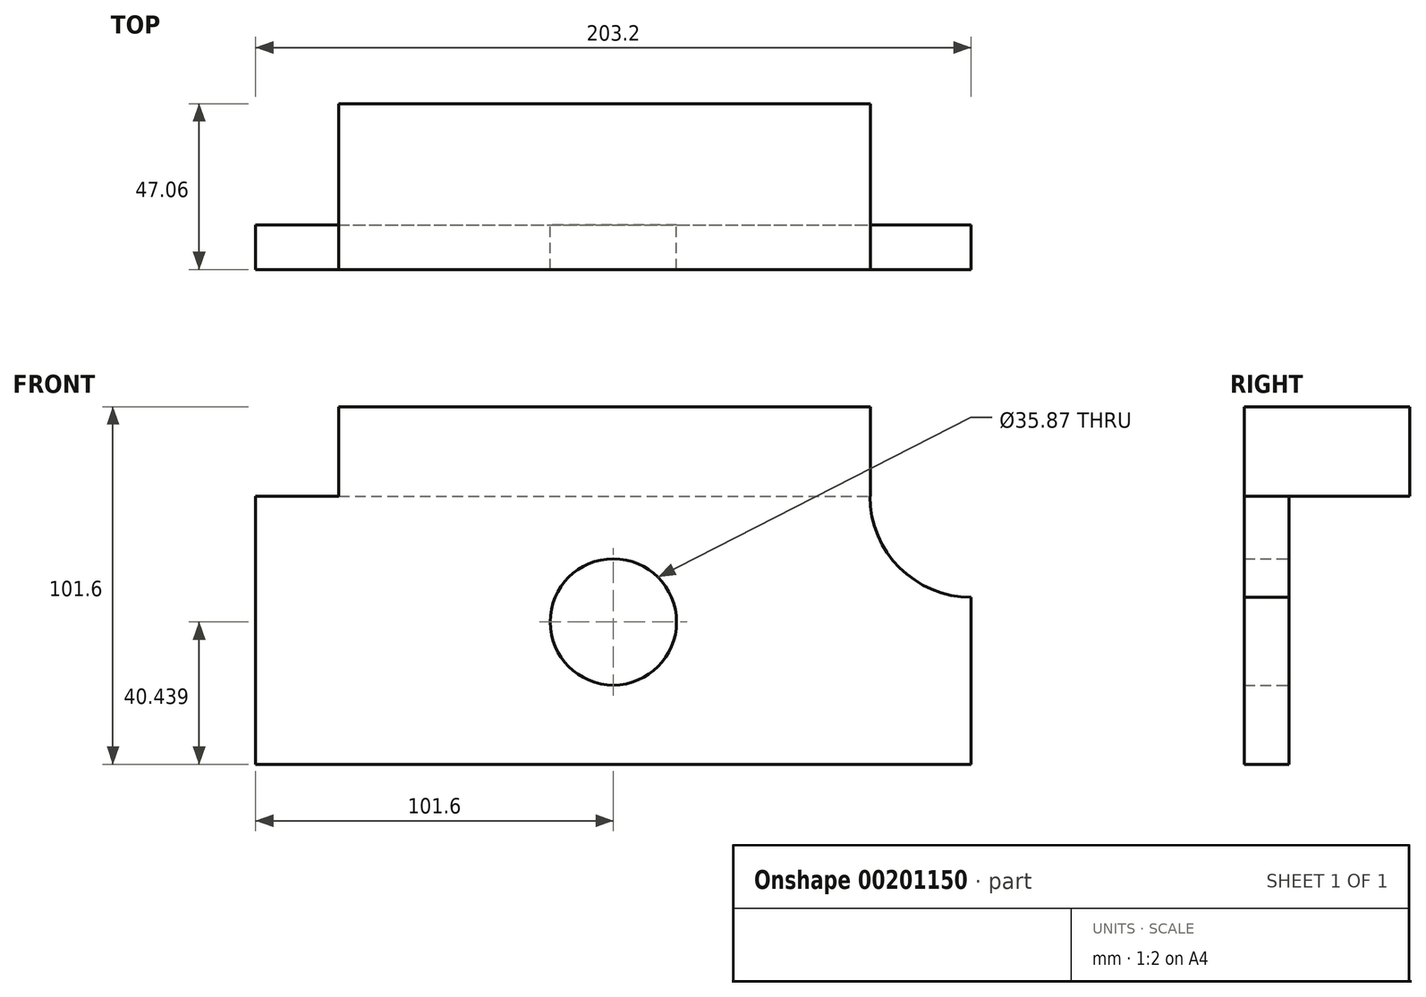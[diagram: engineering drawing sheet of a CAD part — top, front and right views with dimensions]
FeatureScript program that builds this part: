
annotation { "Feature Type Name" : "Feature", "Feature Type Description" : "" }
export const myFeature = defineFeature(function(context is Context, id is Id, definition is map)
    precondition{}
    {
        {
            var Q0;
            Q0=qCreatedBy(makeId("Front.planeOp"),FACE);
            var sketch = newSketch(context, id + "F0", { "sketchPlane" : qUnion([Q0])});
            skLineSegment(sketch, "E0.bottom", {"start": v(-101.6, 16.7) * mm, "end": v(72.84, 16.7) * mm});
            skLineSegment(sketch, "E0.top", {"start": v(-101.6, -59.5) * mm, "end": v(101.6, -59.5) * mm});
            skLineSegment(sketch, "E0.left", {"start": v(-101.6, 16.7) * mm, "end": v(-101.6, -59.5) * mm});
            skLineSegment(sketch, "E0.right", {"start": v(101.6, -12.05) * mm, "end": v(101.6, -59.5) * mm});
            skCircle(sketch, "E1", {"center": v(0, -19.05) * mm, "radius": 17.94 * mm});
            skPoint(sketch, "E2.orphan", {"position": v(0, -16) * mm});
            skPoint(sketch, "E3.end.orphan", {"position": v(0, -59.5) * mm});
            skPoint(sketch, "E4.end.orphan", {"position": v(0, 16.7) * mm});
            skArc(sketch, "E5", {"start": v(72.84, 16.7) * mm, "mid": v(81.26, -3.63) * mm, "end": v(101.6, -12.05) * mm});
            skSolve(sketch);
        }
        {
            var Q0;
            Q0 = qSketchRegion(id + "F0", true);
            extrude(context, id + "F1", {"entities" : qUnion([Q0]), "depth" : 12.7 * mm});
        }
        {
            var Q0;
            Q0=makeQuery(id+"F1.opExtrude","SWEPT_FACE",FACE,{"disambiguationData":[OSD([sQuery(id+"F0.wireOp",EDGE,"E0.bottom")])]});
            var sketch = newSketch(context, id + "F2", { "sketchPlane" : qUnion([Q0])});
            skLineSegment(sketch, "E6.bottom", {"start": v(-77.95, -12.7) * mm, "end": v(73.01, -12.7) * mm});
            skLineSegment(sketch, "E6.top", {"start": v(-77.95, 34.36) * mm, "end": v(73.01, 34.36) * mm});
            skLineSegment(sketch, "E6.left", {"start": v(-77.95, -12.7) * mm, "end": v(-77.95, 34.36) * mm});
            skLineSegment(sketch, "E6.right", {"start": v(73.01, -12.7) * mm, "end": v(73.01, 34.36) * mm});
            skSolve(sketch);
        }
        {
            var Q0;
            Q0 = qSketchRegion(id + "F2", true);
            extrude(context, id + "F3", {"entities" : qUnion([Q0]), "operationType" : NewBodyOperationType.ADD, "depth" : 25.4 * mm});
        }
    });
